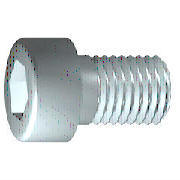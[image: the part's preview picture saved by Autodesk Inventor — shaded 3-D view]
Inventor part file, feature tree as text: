
AUTODESK INVENTOR PART (.ipt)
format: ipt  version: 2024.3 (Build 283343000, 343)  size: 190,976 bytes
history: native  units: mm (DEFAULTED — no unit token found)
features: extrude x1, plane x1, fillet x1
ambient origin geometry x7: Origin, YZ Plane, XY Plane, X Axis, Y Axis, Z Axis, Center Point
bodies: Solid1 (feature_tree), Body (feature_tree)
feature tree (3):
  extrude  "Slot"  Depth=14.25mm
  plane  "Work Plane1"
  fillet  "Fillet2"  Radius=0.429515mm
